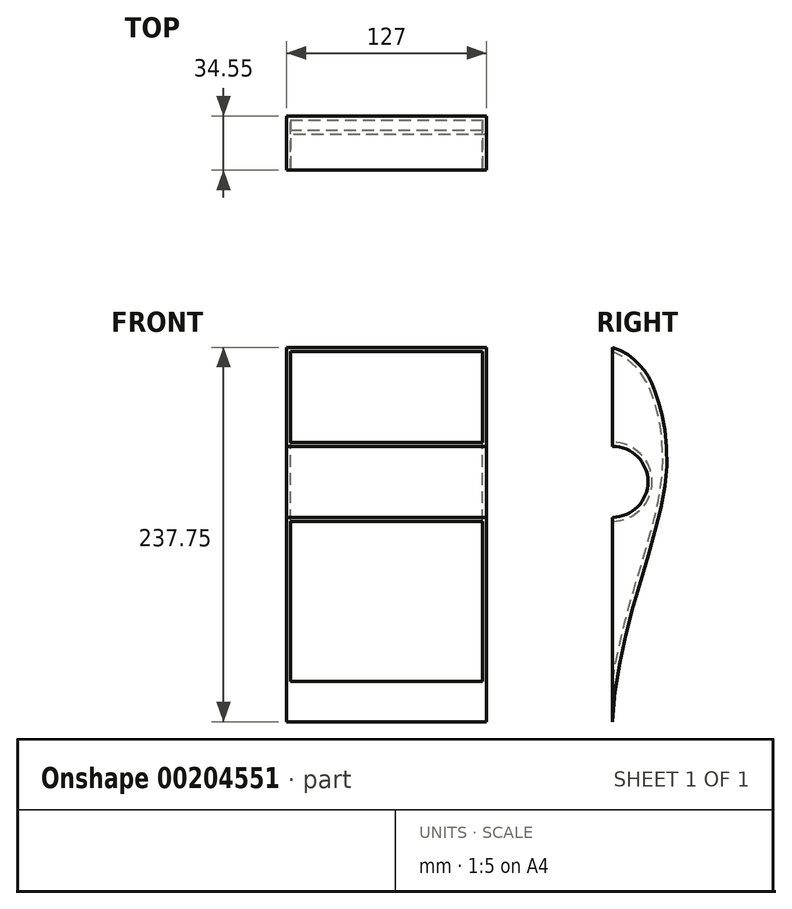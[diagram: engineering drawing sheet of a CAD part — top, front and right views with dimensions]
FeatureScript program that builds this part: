
annotation { "Feature Type Name" : "Feature", "Feature Type Description" : "" }
export const myFeature = defineFeature(function(context is Context, id is Id, definition is map)
    precondition{}
    {
        {
            var Q0;
            Q0=qCreatedBy(makeId("Right.planeOp"),FACE);
            var sketch = newSketch(context, id + "F0", { "sketchPlane" : qUnion([Q0])});
            skLineSegment(sketch, "E0", {"start": v(-8.41, 34.5) * mm, "end": v(-8.41, -117.9) * mm, "construction": true});
            skFitSpline(sketch, "E1", {"points": [v(-8.41, -117.9) * mm, v(25.26, 34.5) * mm, v(19.32, 90.23) * mm, v(12.99, 103.3) * mm, v(4.92, 112.57) * mm, v(-8.41, 119.85) * mm], "startDerivative": vector(20.84, 442.04) * mm, "endDerivative": vector(-119.7, 35.88) * mm});
            skLineSegment(sketch, "E2", {"start": v(-8.41, 119.85) * mm, "end": v(-8.41, -117.9) * mm});
            skArc(sketch, "E3", {"start": v(-8.41, 11.95) * mm, "mid": v(14.14, 34.5) * mm, "end": v(-8.41, 57.05) * mm});
            skSolve(sketch);
        }
        {
            var Q0;
            {var subQ0=sQuery(id+"F0.wireOp",EDGE,"E1");Q0=makeQuery(id+"F0.imprint","IMPRINT",FACE,{"disambiguationData":[TD([[makeQuery(id+"F0.imprint","IMPRINT",EDGE,{"derivedFrom":subQ0}),1.0]])]});}
            extrude(context, id + "F1", {"entities" : qUnion([Q0]), "endBound" : BoundingType.SYMMETRIC, "depth" : 127 * mm});
        }
        {
            var Q0;
            {var subQ0=sQuery(id+"F0.wireOp",EDGE,"E2");Q0=makeQuery(id+"F1.opExtrude","SWEPT_FACE",FACE,{"disambiguationData":[OSD([subQ0]),TDD([makeQuery(id+"F0.imprint","IMPRINT",EDGE,{"disambiguationData":[TD([[makeQuery(id+"F0.imprint","INTERSECT",VERTEX,{"disambiguationData":[OD(0.0)],"derivedFrom":[sQuery(id+"F0.wireOp",EDGE,"E1"),subQ0]}),1.0]])],"derivedFrom":subQ0})])]});}
            var Q1;
            {var subQ0=sQuery(id+"F0.wireOp",EDGE,"E2");Q1=makeQuery(id+"F1.opExtrude","SWEPT_FACE",FACE,{"disambiguationData":[OSD([subQ0]),TDD([makeQuery(id+"F0.imprint","IMPRINT",EDGE,{"disambiguationData":[TD([[makeQuery(id+"F0.imprint","INTERSECT",VERTEX,{"disambiguationData":[OD(1.0)],"derivedFrom":[sQuery(id+"F0.wireOp",EDGE,"E1"),subQ0]}),-1.0]])],"derivedFrom":subQ0})])]});}
            shell(context, id + "F2", {"entities" : qUnion([Q0, Q1]), "thickness" : 2.54 * mm});
        }
    });
